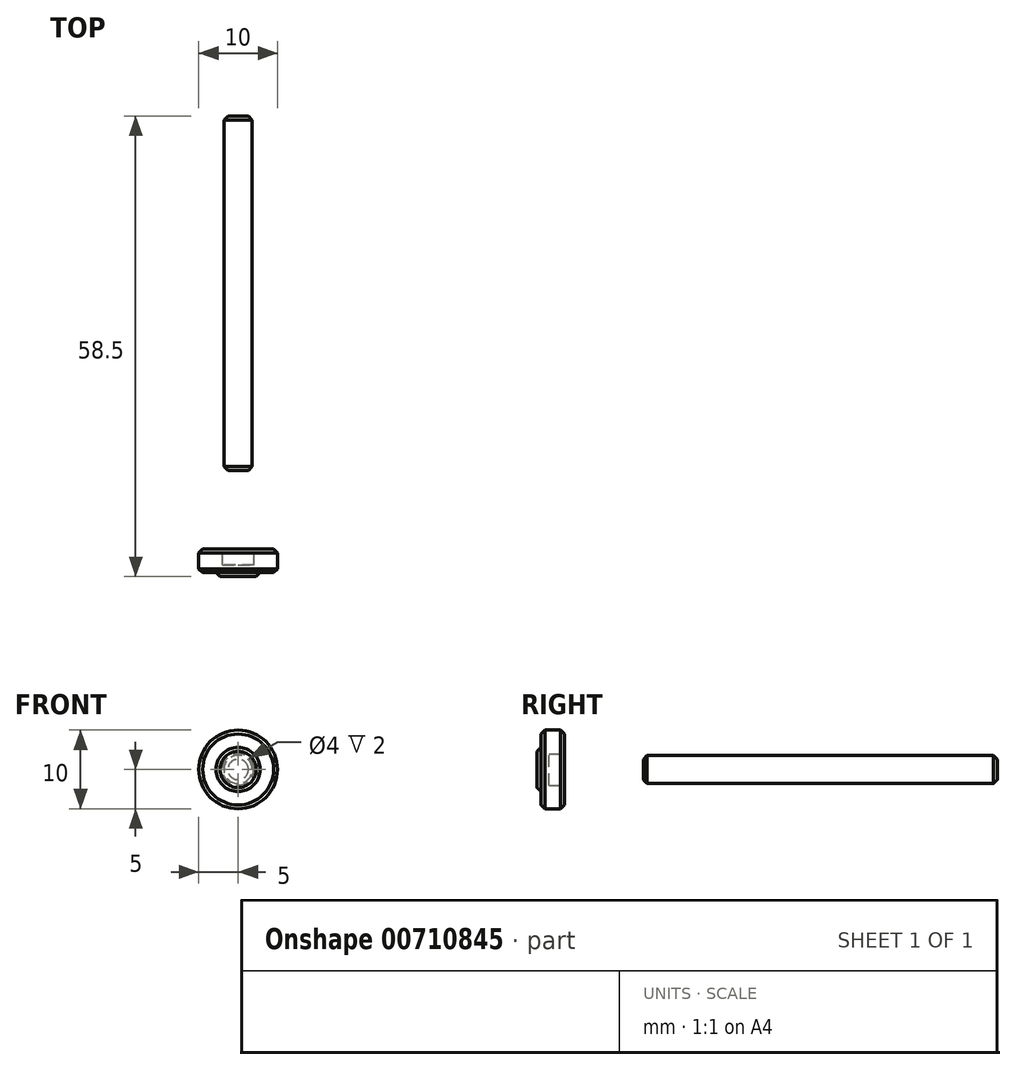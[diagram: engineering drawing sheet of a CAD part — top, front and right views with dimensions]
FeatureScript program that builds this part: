
annotation { "Feature Type Name" : "Feature", "Feature Type Description" : "" }
export const myFeature = defineFeature(function(context is Context, id is Id, definition is map)
    precondition{}
    {
        {
            var Q0;
            Q0=qCreatedBy(makeId("Front.planeOp"),FACE);
            var sketch = newSketch(context, id + "F0", { "sketchPlane" : qUnion([Q0])});
            skCircle(sketch, "E0", {"center": v(0, 0) * mm, "radius": 2 * mm});
            skCircle(sketch, "E1", {"center": v(0, 0) * mm, "radius": 5 * mm});
            skCircle(sketch, "E2", {"center": v(0, 0) * mm, "radius": 2.8 * mm});
            skCircle(sketch, "E3.0", {"center": v(0, 0) * mm, "radius": 1.8 * mm});
            skSolve(sketch);
        }
        {
            var Q0;
            Q0=makeQuery(id+"F0.imprint","IMPRINT",FACE,{"disambiguationData":[TD([[makeQuery(id+"F0.imprint","IMPRINT",EDGE,{"derivedFrom":sQuery(id+"F0.wireOp",EDGE,"E1")}),1.0]])]});
            extrude(context, id + "F1", {"entities" : qUnion([Q0]), "depth" : 3 * mm, "offsetDistance" : 25 * mm});
        }
        {
            var Q0;
            Q0=makeQuery(id+"F0.imprint","IMPRINT",FACE,{"disambiguationData":[TD([[makeQuery(id+"F0.imprint","IMPRINT",EDGE,{"derivedFrom":sQuery(id+"F0.wireOp",EDGE,"E0")}),-1.0]])]});
            var Q1;
            Q1=makeQuery(id+"F0.imprint","IMPRINT",FACE,{"disambiguationData":[TD([[makeQuery(id+"F0.imprint","IMPRINT",EDGE,{"derivedFrom":sQuery(id+"F0.wireOp",EDGE,"E0")}),1.0]])]});
            var Q2;
            Q2=makeQuery(id+"F0.imprint","IMPRINT",FACE,{"disambiguationData":[TD([[makeQuery(id+"F0.imprint","IMPRINT",EDGE,{"derivedFrom":sQuery(id+"F0.wireOp",EDGE,"E3.0")}),1.0]])]});
            extrude(context, id + "F2", {"entities" : qUnion([Q0, Q1, Q2]), "operationType" : NewBodyOperationType.ADD, "depth" : 3.5 * mm, "offsetDistance" : 25 * mm});
        }
        {
            var Q0;
            Q0=makeQuery(id+"F0.imprint","IMPRINT",FACE,{"disambiguationData":[TD([[makeQuery(id+"F0.imprint","IMPRINT",EDGE,{"derivedFrom":sQuery(id+"F0.wireOp",EDGE,"E0")}),1.0]])]});
            var Q1;
            Q1=makeQuery(id+"F0.imprint","IMPRINT",FACE,{"disambiguationData":[TD([[makeQuery(id+"F0.imprint","IMPRINT",EDGE,{"derivedFrom":sQuery(id+"F0.wireOp",EDGE,"E3.0")}),1.0]])]});
            extrude(context, id + "F3", {"entities" : qUnion([Q0, Q1]), "operationType" : NewBodyOperationType.REMOVE, "depth" : 2 * mm, "offsetDistance" : 25 * mm});
        }
        {
            var Q0;
            Q0=makeQuery(id+"F2.opExtrude","CAP_EDGE",EDGE,{"disambiguationData":[OSD([sQuery(id+"F0.wireOp",EDGE,"E2")])],"isStart":false});
            var Q1;
            Q1=makeQuery(id+"F1.opExtrude","CAP_EDGE",EDGE,{"disambiguationData":[OSD([sQuery(id+"F0.wireOp",EDGE,"E1")])],"isStart":false});
            var Q2;
            Q2=makeQuery(id+"F1.opExtrude","CAP_EDGE",EDGE,{"disambiguationData":[OSD([sQuery(id+"F0.wireOp",EDGE,"E1")])],"isStart":true});
            chamfer(context, id + "F4", {"entities" : qUnion([Q0, Q1, Q2]), "width" : .5 * mm, "tangentPropagation" : true});
        }
        {
            var Q0;
            Q0=makeQuery(id+"F0.imprint","IMPRINT",FACE,{"disambiguationData":[TD([[makeQuery(id+"F0.imprint","IMPRINT",EDGE,{"derivedFrom":sQuery(id+"F0.wireOp",EDGE,"E3.0")}),1.0]])]});
            extrude(context, id + "F5", {"entities" : qUnion([Q0]), "oppositeDirection" : true, "depth" : 55 * mm, "offsetDistance" : 25 * mm, "hasSecondDirection" : true, "secondDirectionOppositeDirection" : true, "secondDirectionDepth" : 10 * mm});
        }
        {
            var Q0;
            Q0=makeQuery(id+"F5.opExtrude","CAP_EDGE",EDGE,{"disambiguationData":[OSD([sQuery(id+"F0.wireOp",EDGE,"E3.0")])],"isStart":false});
            var Q1;
            Q1=makeQuery(id+"F5.opExtrude","CAP_EDGE",EDGE,{"disambiguationData":[OSD([sQuery(id+"F0.wireOp",EDGE,"E3.0")])],"isStart":true});
            chamfer(context, id + "F6", {"entities" : qUnion([Q0, Q1]), "width" : .5 * mm, "tangentPropagation" : true});
        }
    });
